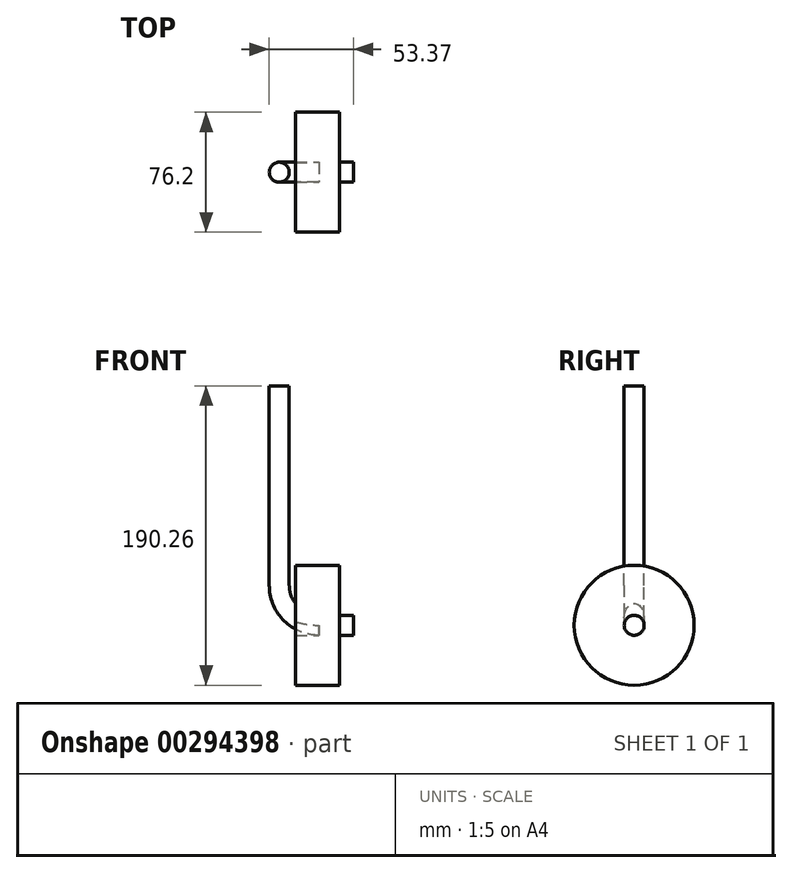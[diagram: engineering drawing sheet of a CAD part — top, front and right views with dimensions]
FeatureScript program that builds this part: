
annotation { "Feature Type Name" : "Feature", "Feature Type Description" : "" }
export const myFeature = defineFeature(function(context is Context, id is Id, definition is map)
    precondition{}
    {
        {
            var Q0;
            Q0=qCreatedBy(makeId("Top.planeOp"),FACE);
            var sketch = newSketch(context, id + "F0", { "sketchPlane" : qUnion([Q0])});
            skCircle(sketch, "E0", {"center": v(0, 0) * mm, "radius": 6.35 * mm});
            skSolve(sketch);
        }
        {
            var Q0;
            Q0 = qSketchRegion(id + "F0", true);
            extrude(context, id + "F1", {"entities" : qUnion([Q0]), "oppositeDirection" : true, "depth" : 101.6 * mm, "offsetDistance" : 25.4 * mm});
        }
        {
            var Q0;
            Q0=qCreatedBy(makeId("Front.planeOp"),FACE);
            var sketch = newSketch(context, id + "F2", { "sketchPlane" : qUnion([Q0])});
            skLineSegment(sketch, "E1.top", {"start": v(25.4, -152.16) * mm, "end": v(38.38, -152.16) * mm});
            skLineSegment(sketch, "E1.left", {"start": v(0, -100.06) * mm, "end": v(0, -126.76) * mm});
            skPoint(sketch, "E2.visualSharp", {"position": v(0, -152.16) * mm});
            skArc(sketch, "E2.filletArc", {"start": v(0, -126.76) * mm, "mid": v(7.44, -144.72) * mm, "end": v(25.4, -152.16) * mm});
            skSolve(sketch);
        }
        {
            var Q0;
            Q0=makeQuery(id+"F1.opExtrude","CAP_FACE",FACE,{"disambiguationData":[OSD([sQuery(id+"F0.wireOp",EDGE,"E0")])],"isStart":false});
            var Q1;
            Q1=sQuery(id+"F2.wireOp",EDGE,"E1.left");
            var Q2;
            Q2=sQuery(id+"F2.wireOp",EDGE,"E2.filletArc");
            var Q3;
            Q3=sQuery(id+"F2.wireOp",EDGE,"E1.top");
            sweep(context, id + "F3", {"operationType" : NewBodyOperationType.ADD, "profiles" : qUnion([Q0]), "path" : qUnion([Q1, Q2, Q3])});
        }
        {
            var Q0;
            Q0=makeQuery(id+"F3.opSweep","CAP_FACE",FACE,{"disambiguationData":[OSD([sQuery(id+"F0.wireOp",EDGE,"E0"),sQuery(id+"F2.wireOp",VERTEX,"E1.top.end")])],"isStart":false});
            var sketch = newSketch(context, id + "F4", { "sketchPlane" : qUnion([Q0])});
            skCircle(sketch, "E3", {"center": v(0, -152.16) * mm, "radius": 6.35 * mm});
            skCircle(sketch, "E4", {"center": v(0, -152.16) * mm, "radius": 38.1 * mm});
            skSolve(sketch);
        }
        {
            var Q0;
            Q0=makeQuery(id+"F4.imprint","IMPRINT",FACE,{"disambiguationData":[TD([[makeQuery(id+"F4.imprint","IMPRINT",EDGE,{"derivedFrom":sQuery(id+"F4.wireOp",EDGE,"E3")}),-1.0]])]});
            extrude(context, id + "F5", {"entities" : qUnion([Q0]), "oppositeDirection" : true, "depth" : 28.2 * mm, "offsetDistance" : 25.4 * mm});
        }
        {
            var Q0;
            Q0=makeQuery(id+"F5.boolean.opBoolean","MERGE",FACE,{"derivedFrom":[makeQuery(id+"F3.opSweep","CAP_FACE",FACE,{"disambiguationData":[OSD([sQuery(id+"F0.wireOp",EDGE,"E0"),sQuery(id+"F2.wireOp",VERTEX,"E1.top.end")])],"isStart":false}),makeQuery(id+"F5.opExtrude","CAP_FACE",FACE,{"disambiguationData":[OSD([sQuery(id+"F4.wireOp",EDGE,"E3"),sQuery(id+"F4.wireOp",EDGE,"E4")])],"isStart":true})]});
            var sketch = newSketch(context, id + "F6", { "sketchPlane" : qUnion([Q0])});
            skCircle(sketch, "E5", {"center": v(0, -152.16) * mm, "radius": 6.35 * mm});
            skSolve(sketch);
        }
        {
            var Q0;
            Q0 = qSketchRegion(id + "F6", true);
            extrude(context, id + "F7", {"entities" : qUnion([Q0]), "operationType" : NewBodyOperationType.ADD, "depth" : 8.64 * mm, "offsetDistance" : 25.4 * mm});
        }
    });
